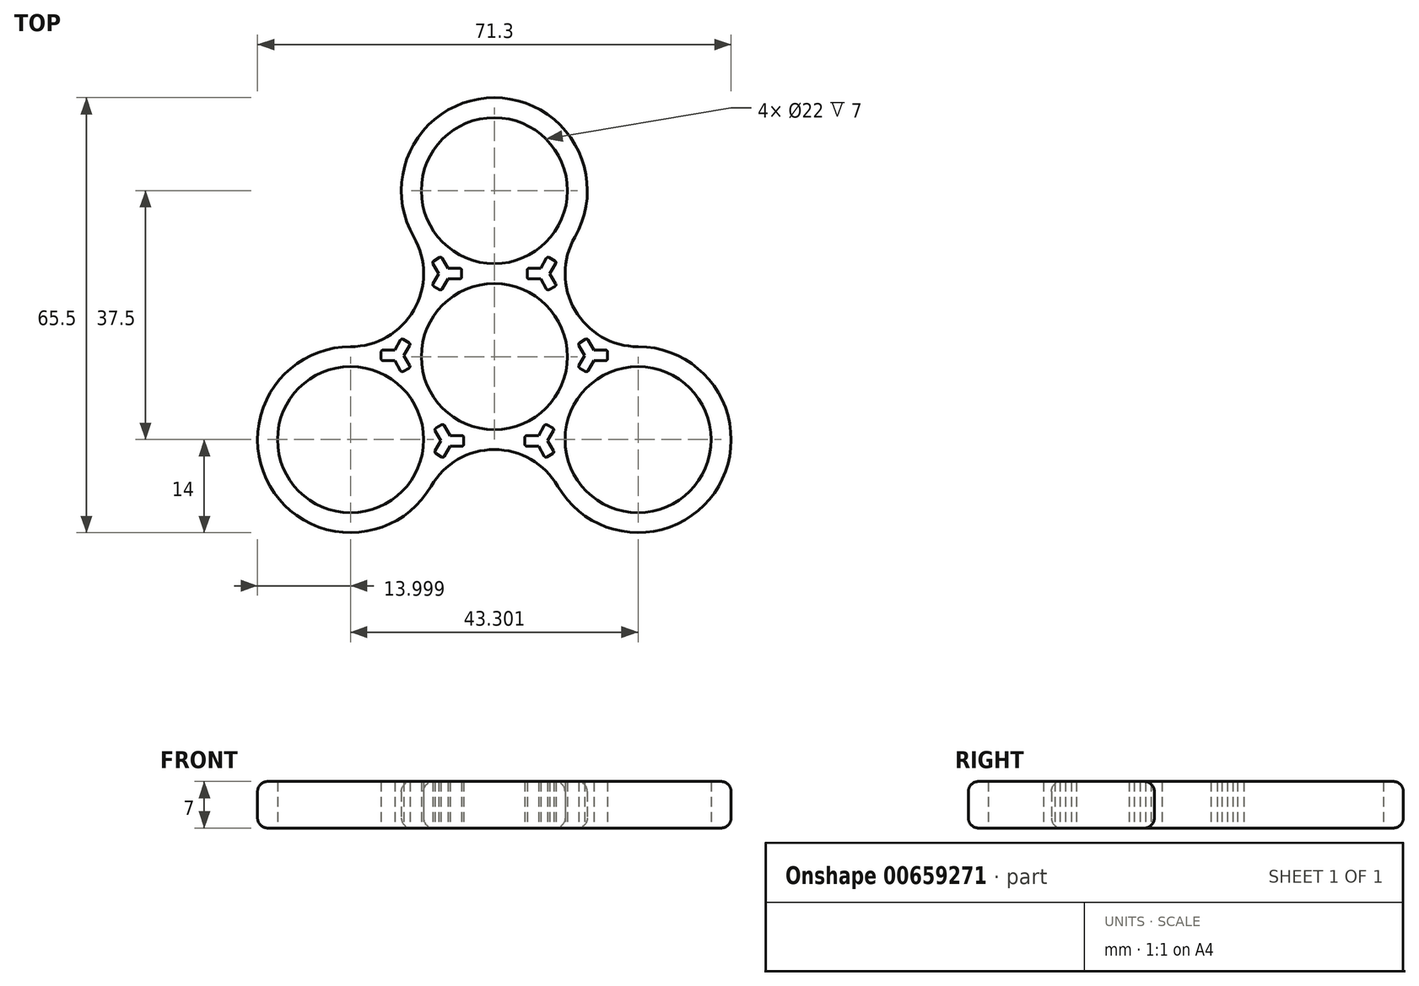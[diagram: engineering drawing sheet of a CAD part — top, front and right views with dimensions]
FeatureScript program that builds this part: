
annotation { "Feature Type Name" : "Feature", "Feature Type Description" : "" }
export const myFeature = defineFeature(function(context is Context, id is Id, definition is map)
    precondition{}
    {
        {
            var Q0;
            Q0=qCreatedBy(makeId("Top.planeOp"),FACE);
            var sketch = newSketch(context, id + "F0", { "sketchPlane" : qUnion([Q0])});
            skCircle(sketch, "E0", {"center": v(0, 0) * mm, "radius": 11 * mm});
            skCircle(sketch, "E1", {"center": v(0, 25) * mm, "radius": 11 * mm});
            skArc(sketch, "E2.0", {"start": v(12.12, 18) * mm, "mid": v(0, 39) * mm, "end": v(-12.12, 18) * mm});
            skArc(sketch, "E3.1.0", {"start": v(-21.65, 1.5) * mm, "mid": v(-33.77, -19.5) * mm, "end": v(-9.53, -19.5) * mm});
            skCircle(sketch, "E3.1.1", {"center": v(-21.65, -12.5) * mm, "radius": 11 * mm});
            skArc(sketch, "E3.2.0", {"start": v(9.53, -19.5) * mm, "mid": v(33.77, -19.5) * mm, "end": v(21.65, 1.5) * mm});
            skCircle(sketch, "E3.2.1", {"center": v(21.65, -12.5) * mm, "radius": 11 * mm});
            skArc(sketch, "E4", {"start": v(12.12, 18) * mm, "mid": v(12.12, 7) * mm, "end": v(21.65, 1.5) * mm});
            skArc(sketch, "E5.1.0", {"start": v(-21.65, 1.5) * mm, "mid": v(-12.12, 7) * mm, "end": v(-12.12, 18) * mm});
            skArc(sketch, "E5.2.0", {"start": v(9.53, -19.5) * mm, "mid": v(0, -14) * mm, "end": v(-9.53, -19.5) * mm});
            skLineSegment(sketch, "E6", {"start": v(0, 11) * mm, "end": v(0, 14) * mm});
            skLineSegment(sketch, "E7", {"start": v(4.94, 12.5) * mm, "end": v(4.94, 13.02) * mm});
            skLineSegment(sketch, "E8", {"start": v(5.21, 13.3) * mm, "end": v(6.97, 13.3) * mm});
            skLineSegment(sketch, "E9.MirrorCS", {"start": v(5.21, 11.7) * mm, "end": v(6.97, 11.7) * mm});
            skLineSegment(sketch, "E10.MirrorCS", {"start": v(4.94, 12.5) * mm, "end": v(4.94, 11.98) * mm});
            skPoint(sketch, "E11.visualSharp", {"position": v(4.94, 13.3) * mm});
            skArc(sketch, "E11.filletArc", {"start": v(5.21, 13.3) * mm, "mid": v(5.02, 13.22) * mm, "end": v(4.94, 13.02) * mm});
            skArc(sketch, "E12.MirrorCS", {"start": v(5.21, 11.7) * mm, "mid": v(5.02, 11.78) * mm, "end": v(4.94, 11.98) * mm});
            skPoint(sketch, "E13.orphan", {"position": v(4.94, 11.7) * mm});
            skLineSegment(sketch, "E14.1.0", {"start": v(7.85, 10.17) * mm, "end": v(6.97, 11.7) * mm});
            skArc(sketch, "E14.1.1", {"start": v(7.85, 10.17) * mm, "mid": v(8.02, 10.05) * mm, "end": v(8.23, 10.07) * mm});
            skLineSegment(sketch, "E14.1.2", {"start": v(8.69, 10.33) * mm, "end": v(8.23, 10.07) * mm});
            skLineSegment(sketch, "E14.1.3", {"start": v(8.69, 10.33) * mm, "end": v(9.14, 10.6) * mm});
            skArc(sketch, "E14.1.4", {"start": v(9.24, 10.97) * mm, "mid": v(9.27, 10.76) * mm, "end": v(9.14, 10.6) * mm});
            skLineSegment(sketch, "E14.1.5", {"start": v(9.24, 10.97) * mm, "end": v(8.36, 12.5) * mm});
            skLineSegment(sketch, "E14.2.0", {"start": v(9.24, 14.03) * mm, "end": v(8.36, 12.5) * mm});
            skArc(sketch, "E14.2.1", {"start": v(9.24, 14.03) * mm, "mid": v(9.27, 14.24) * mm, "end": v(9.14, 14.4) * mm});
            skLineSegment(sketch, "E14.2.2", {"start": v(8.69, 14.67) * mm, "end": v(9.14, 14.4) * mm});
            skLineSegment(sketch, "E14.2.3", {"start": v(8.69, 14.67) * mm, "end": v(8.23, 14.93) * mm});
            skArc(sketch, "E14.2.4", {"start": v(7.85, 14.83) * mm, "mid": v(8.02, 14.95) * mm, "end": v(8.23, 14.93) * mm});
            skLineSegment(sketch, "E14.2.5", {"start": v(7.85, 14.83) * mm, "end": v(6.97, 13.3) * mm});
            skArc(sketch, "E15.MirrorCS", {"start": v(-7.85, 14.83) * mm, "mid": v(-8.02, 14.95) * mm, "end": v(-8.23, 14.93) * mm});
            skLineSegment(sketch, "E16.MirrorCS", {"start": v(-8.69, 10.33) * mm, "end": v(-8.23, 10.07) * mm});
            skArc(sketch, "E17.MirrorCS", {"start": v(-7.85, 10.17) * mm, "mid": v(-8.02, 10.05) * mm, "end": v(-8.23, 10.07) * mm});
            skArc(sketch, "E18.MirrorCS", {"start": v(-9.24, 10.97) * mm, "mid": v(-9.27, 10.76) * mm, "end": v(-9.14, 10.6) * mm});
            skLineSegment(sketch, "E19.MirrorCS", {"start": v(-8.69, 10.33) * mm, "end": v(-9.14, 10.6) * mm});
            skLineSegment(sketch, "E20.MirrorCS", {"start": v(-8.69, 14.67) * mm, "end": v(-8.23, 14.93) * mm});
            skLineSegment(sketch, "E21.MirrorCS", {"start": v(-8.69, 14.67) * mm, "end": v(-9.14, 14.4) * mm});
            skArc(sketch, "E22.MirrorCS", {"start": v(-9.24, 14.03) * mm, "mid": v(-9.27, 14.24) * mm, "end": v(-9.14, 14.4) * mm});
            skLineSegment(sketch, "E23.MirrorCS", {"start": v(-9.24, 10.97) * mm, "end": v(-8.36, 12.5) * mm});
            skLineSegment(sketch, "E24.MirrorCS", {"start": v(-7.85, 10.17) * mm, "end": v(-6.97, 11.7) * mm});
            skLineSegment(sketch, "E25.MirrorCS", {"start": v(-7.85, 14.83) * mm, "end": v(-6.97, 13.3) * mm});
            skLineSegment(sketch, "E26.MirrorCS", {"start": v(-9.24, 14.03) * mm, "end": v(-8.36, 12.5) * mm});
            skLineSegment(sketch, "E27.MirrorCS", {"start": v(-5.21, 13.3) * mm, "end": v(-6.97, 13.3) * mm});
            skLineSegment(sketch, "E28.MirrorCS", {"start": v(-5.21, 11.7) * mm, "end": v(-6.97, 11.7) * mm});
            skArc(sketch, "E29.MirrorCS", {"start": v(-5.21, 11.7) * mm, "mid": v(-5.02, 11.78) * mm, "end": v(-4.94, 11.98) * mm});
            skLineSegment(sketch, "E30.MirrorCS", {"start": v(-4.94, 12.5) * mm, "end": v(-4.94, 11.98) * mm});
            skLineSegment(sketch, "E31.MirrorCS", {"start": v(-4.94, 12.5) * mm, "end": v(-4.94, 13.02) * mm});
            skArc(sketch, "E32.MirrorCS", {"start": v(-5.21, 13.3) * mm, "mid": v(-5.02, 13.22) * mm, "end": v(-4.94, 13.02) * mm});
            skLineSegment(sketch, "E33.1.0", {"start": v(-13.3, 2.35) * mm, "end": v(-12.84, 2.1) * mm});
            skLineSegment(sketch, "E33.1.1", {"start": v(-13.3, 2.35) * mm, "end": v(-13.75, 2.62) * mm});
            skLineSegment(sketch, "E33.1.2", {"start": v(-16.77, 0.99) * mm, "end": v(-15, 0.99) * mm});
            skLineSegment(sketch, "E33.1.3", {"start": v(-12.74, -1.34) * mm, "end": v(-13.62, 0.19) * mm});
            skLineSegment(sketch, "E33.1.4", {"start": v(-14.12, 2.52) * mm, "end": v(-15, 0.99) * mm});
            skLineSegment(sketch, "E33.1.5", {"start": v(-12.74, 1.72) * mm, "end": v(-13.62, 0.19) * mm});
            skLineSegment(sketch, "E33.1.6", {"start": v(-14.12, -2.14) * mm, "end": v(-15, -0.61) * mm});
            skLineSegment(sketch, "E33.1.7", {"start": v(-16.77, -0.61) * mm, "end": v(-15, -0.61) * mm});
            skArc(sketch, "E33.1.9", {"start": v(-12.74, 1.72) * mm, "mid": v(-12.71, 1.92) * mm, "end": v(-12.84, 2.1) * mm});
            skArc(sketch, "E33.1.11", {"start": v(-14.12, 2.52) * mm, "mid": v(-13.96, 2.64) * mm, "end": v(-13.75, 2.62) * mm});
            skArc(sketch, "E33.1.15", {"start": v(-16.77, 0.99) * mm, "mid": v(-16.96, 0.9) * mm, "end": v(-17.04, 0.71) * mm});
            skLineSegment(sketch, "E33.1.16", {"start": v(-17.04, 0.19) * mm, "end": v(-17.04, 0.71) * mm});
            skLineSegment(sketch, "E33.1.17", {"start": v(-17.04, 0.19) * mm, "end": v(-17.04, -0.34) * mm});
            skArc(sketch, "E33.1.18", {"start": v(-16.77, -0.61) * mm, "mid": v(-16.96, -0.53) * mm, "end": v(-17.04, -0.34) * mm});
            skLineSegment(sketch, "E33.1.19", {"start": v(-13.3, -1.98) * mm, "end": v(-13.75, -2.24) * mm});
            skArc(sketch, "E33.1.20", {"start": v(-14.12, -2.14) * mm, "mid": v(-13.96, -2.27) * mm, "end": v(-13.75, -2.24) * mm});
            skLineSegment(sketch, "E33.1.21", {"start": v(-13.3, -1.98) * mm, "end": v(-12.84, -1.71) * mm});
            skArc(sketch, "E33.1.22", {"start": v(-12.74, -1.34) * mm, "mid": v(-12.71, -1.55) * mm, "end": v(-12.84, -1.71) * mm});
            skLineSegment(sketch, "E33.1.23", {"start": v(-7.53, -15.02) * mm, "end": v(-6.65, -13.49) * mm});
            skArc(sketch, "E33.1.24", {"start": v(-4.88, -13.49) * mm, "mid": v(-4.69, -13.4) * mm, "end": v(-4.6, -13.21) * mm});
            skArc(sketch, "E33.1.25", {"start": v(-7.53, -15.02) * mm, "mid": v(-7.7, -15.14) * mm, "end": v(-7.9, -15.12) * mm});
            skLineSegment(sketch, "E33.1.26", {"start": v(-8.36, -14.85) * mm, "end": v(-8.81, -14.6) * mm});
            skLineSegment(sketch, "E33.1.27", {"start": v(-8.36, -14.85) * mm, "end": v(-7.9, -15.12) * mm});
            skLineSegment(sketch, "E33.1.28", {"start": v(-7.53, -10.36) * mm, "end": v(-6.65, -11.89) * mm});
            skLineSegment(sketch, "E33.1.29", {"start": v(-4.6, -12.69) * mm, "end": v(-4.6, -12.16) * mm});
            skLineSegment(sketch, "E33.1.30", {"start": v(-8.91, -14.22) * mm, "end": v(-8.03, -12.69) * mm});
            skLineSegment(sketch, "E33.1.31", {"start": v(-4.88, -13.49) * mm, "end": v(-6.65, -13.49) * mm});
            skLineSegment(sketch, "E33.1.32", {"start": v(-4.6, -12.69) * mm, "end": v(-4.6, -13.21) * mm});
            skLineSegment(sketch, "E33.1.33", {"start": v(-4.88, -11.89) * mm, "end": v(-6.65, -11.89) * mm});
            skLineSegment(sketch, "E33.1.34", {"start": v(-8.91, -11.16) * mm, "end": v(-8.03, -12.69) * mm});
            skArc(sketch, "E33.1.35", {"start": v(-8.91, -14.22) * mm, "mid": v(-8.94, -14.42) * mm, "end": v(-8.81, -14.6) * mm});
            skArc(sketch, "E33.1.36", {"start": v(-8.91, -11.16) * mm, "mid": v(-8.94, -10.95) * mm, "end": v(-8.81, -10.79) * mm});
            skLineSegment(sketch, "E33.1.37", {"start": v(-8.36, -10.52) * mm, "end": v(-8.81, -10.79) * mm});
            skLineSegment(sketch, "E33.1.38", {"start": v(-8.36, -10.52) * mm, "end": v(-7.9, -10.26) * mm});
            skArc(sketch, "E33.1.39", {"start": v(-7.53, -10.36) * mm, "mid": v(-7.7, -10.23) * mm, "end": v(-7.9, -10.26) * mm});
            skArc(sketch, "E33.1.40", {"start": v(-4.88, -11.89) * mm, "mid": v(-4.69, -11.97) * mm, "end": v(-4.6, -12.16) * mm});
            skLineSegment(sketch, "E33.2.0", {"start": v(4.6, -12.69) * mm, "end": v(4.6, -12.16) * mm});
            skLineSegment(sketch, "E33.2.1", {"start": v(4.6, -12.69) * mm, "end": v(4.6, -13.21) * mm});
            skLineSegment(sketch, "E33.2.2", {"start": v(7.53, -15.02) * mm, "end": v(6.65, -13.49) * mm});
            skLineSegment(sketch, "E33.2.3", {"start": v(7.53, -10.36) * mm, "end": v(6.65, -11.89) * mm});
            skLineSegment(sketch, "E33.2.4", {"start": v(4.88, -13.49) * mm, "end": v(6.65, -13.49) * mm});
            skLineSegment(sketch, "E33.2.5", {"start": v(4.88, -11.89) * mm, "end": v(6.65, -11.89) * mm});
            skLineSegment(sketch, "E33.2.6", {"start": v(8.91, -11.16) * mm, "end": v(8.03, -12.69) * mm});
            skLineSegment(sketch, "E33.2.7", {"start": v(8.91, -14.22) * mm, "end": v(8.03, -12.69) * mm});
            skArc(sketch, "E33.2.9", {"start": v(4.88, -11.89) * mm, "mid": v(4.69, -11.97) * mm, "end": v(4.6, -12.16) * mm});
            skArc(sketch, "E33.2.11", {"start": v(4.88, -13.49) * mm, "mid": v(4.69, -13.4) * mm, "end": v(4.6, -13.21) * mm});
            skArc(sketch, "E33.2.15", {"start": v(7.53, -15.02) * mm, "mid": v(7.7, -15.14) * mm, "end": v(7.9, -15.12) * mm});
            skLineSegment(sketch, "E33.2.16", {"start": v(8.36, -14.85) * mm, "end": v(7.9, -15.12) * mm});
            skLineSegment(sketch, "E33.2.17", {"start": v(8.36, -14.85) * mm, "end": v(8.81, -14.6) * mm});
            skArc(sketch, "E33.2.18", {"start": v(8.91, -14.22) * mm, "mid": v(8.94, -14.42) * mm, "end": v(8.81, -14.6) * mm});
            skLineSegment(sketch, "E33.2.19", {"start": v(8.36, -10.52) * mm, "end": v(8.81, -10.79) * mm});
            skArc(sketch, "E33.2.20", {"start": v(8.91, -11.16) * mm, "mid": v(8.94, -10.95) * mm, "end": v(8.81, -10.79) * mm});
            skLineSegment(sketch, "E33.2.21", {"start": v(8.36, -10.52) * mm, "end": v(7.9, -10.26) * mm});
            skArc(sketch, "E33.2.22", {"start": v(7.53, -10.36) * mm, "mid": v(7.7, -10.23) * mm, "end": v(7.9, -10.26) * mm});
            skLineSegment(sketch, "E33.2.23", {"start": v(16.77, 0.99) * mm, "end": v(15, 0.99) * mm});
            skArc(sketch, "E33.2.24", {"start": v(14.12, 2.52) * mm, "mid": v(13.96, 2.64) * mm, "end": v(13.75, 2.62) * mm});
            skArc(sketch, "E33.2.25", {"start": v(16.77, 0.99) * mm, "mid": v(16.96, 0.9) * mm, "end": v(17.04, 0.71) * mm});
            skLineSegment(sketch, "E33.2.26", {"start": v(17.04, 0.19) * mm, "end": v(17.04, -0.34) * mm});
            skLineSegment(sketch, "E33.2.27", {"start": v(17.04, 0.19) * mm, "end": v(17.04, 0.71) * mm});
            skLineSegment(sketch, "E33.2.28", {"start": v(12.74, -1.34) * mm, "end": v(13.62, 0.19) * mm});
            skLineSegment(sketch, "E33.2.29", {"start": v(13.3, 2.35) * mm, "end": v(12.84, 2.1) * mm});
            skLineSegment(sketch, "E33.2.30", {"start": v(16.77, -0.61) * mm, "end": v(15, -0.61) * mm});
            skLineSegment(sketch, "E33.2.31", {"start": v(14.12, 2.52) * mm, "end": v(15, 0.99) * mm});
            skLineSegment(sketch, "E33.2.32", {"start": v(13.3, 2.35) * mm, "end": v(13.75, 2.62) * mm});
            skLineSegment(sketch, "E33.2.33", {"start": v(12.74, 1.72) * mm, "end": v(13.62, 0.19) * mm});
            skLineSegment(sketch, "E33.2.34", {"start": v(14.12, -2.14) * mm, "end": v(15, -0.61) * mm});
            skArc(sketch, "E33.2.35", {"start": v(16.77, -0.61) * mm, "mid": v(16.96, -0.53) * mm, "end": v(17.04, -0.34) * mm});
            skArc(sketch, "E33.2.36", {"start": v(14.12, -2.14) * mm, "mid": v(13.96, -2.27) * mm, "end": v(13.75, -2.24) * mm});
            skLineSegment(sketch, "E33.2.37", {"start": v(13.3, -1.98) * mm, "end": v(13.75, -2.24) * mm});
            skLineSegment(sketch, "E33.2.38", {"start": v(13.3, -1.98) * mm, "end": v(12.84, -1.71) * mm});
            skArc(sketch, "E33.2.39", {"start": v(12.74, -1.34) * mm, "mid": v(12.71, -1.55) * mm, "end": v(12.84, -1.71) * mm});
            skArc(sketch, "E33.2.40", {"start": v(12.74, 1.72) * mm, "mid": v(12.71, 1.92) * mm, "end": v(12.84, 2.1) * mm});
            skSolve(sketch);
        }
        {
            var Q0;
            Q0=makeQuery(id+"F0.imprint","IMPRINT",FACE,{"disambiguationData":[TD([[makeQuery(id+"F0.imprint","IMPRINT",EDGE,{"derivedFrom":sQuery(id+"F0.wireOp",EDGE,"E2.0")}),1.0]])]});
            extrude(context, id + "F1", {"entities" : qUnion([Q0]), "depth" : 7 * mm, "offsetDistance" : 25 * mm});
        }
        {
            var Q0;
            Q0=makeQuery(id+"F1.opExtrude","CAP_EDGE",EDGE,{"disambiguationData":[OSD([sQuery(id+"F0.wireOp",EDGE,"E2.0")])],"isStart":false});
            var Q1;
            Q1=makeQuery(id+"F1.opExtrude","CAP_EDGE",EDGE,{"disambiguationData":[OSD([sQuery(id+"F0.wireOp",EDGE,"E2.0")])],"isStart":true});
            fillet(context, id + "F2", {"entities" : qUnion([Q0, Q1]), "radius" : 1.5 * mm, "tangentPropagation" : true, "allowEdgeOverflow" : false});
        }
    });
